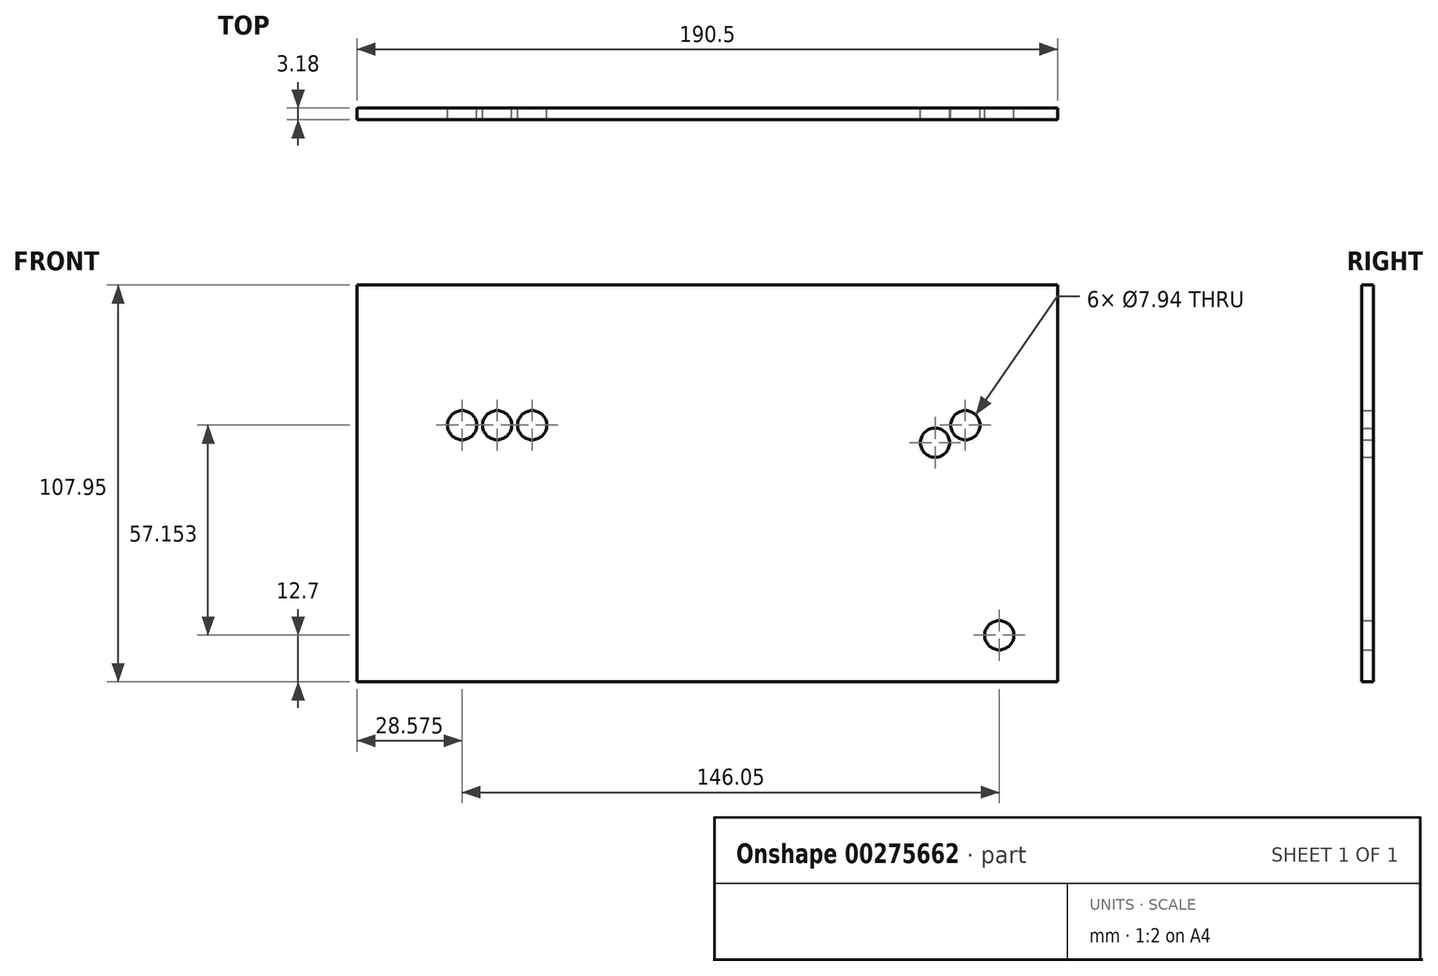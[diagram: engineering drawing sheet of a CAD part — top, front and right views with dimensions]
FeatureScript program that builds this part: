
annotation { "Feature Type Name" : "Feature", "Feature Type Description" : "" }
export const myFeature = defineFeature(function(context is Context, id is Id, definition is map)
    precondition{}
    {
        {
            var Q0;
            Q0=qCreatedBy(makeId("Front.planeOp"),FACE);
            var sketch = newSketch(context, id + "F0", { "sketchPlane" : qUnion([Q0])});
            skLineSegment(sketch, "E0.bottom", {"start": v(0, 0) * mm, "end": v(190.5, 0) * mm});
            skLineSegment(sketch, "E0.top", {"start": v(0, -107.95) * mm, "end": v(190.5, -107.95) * mm});
            skLineSegment(sketch, "E0.left", {"start": v(0, 0) * mm, "end": v(0, -107.95) * mm});
            skLineSegment(sketch, "E0.right", {"start": v(190.5, 0) * mm, "end": v(190.5, -107.95) * mm});
            skLineSegment(sketch, "E1", {"start": v(-10.1, -38.1) * mm, "end": v(60.63, -38.1) * mm, "construction": true});
            skLineSegment(sketch, "E2", {"start": v(38.1, -32.24) * mm, "end": v(38.1, -45.82) * mm, "construction": true});
            skCircle(sketch, "E3", {"center": v(38.1, -38.1) * mm, "radius": 3.97 * mm});
            skLineSegment(sketch, "E4", {"start": v(28.58, -32.24) * mm, "end": v(28.58, -45.82) * mm, "construction": true});
            skCircle(sketch, "E5", {"center": v(28.58, -38.1) * mm, "radius": 3.97 * mm});
            skLineSegment(sketch, "E6", {"start": v(47.63, -32.24) * mm, "end": v(47.63, -45.82) * mm, "construction": true});
            skCircle(sketch, "E7", {"center": v(47.63, -38.1) * mm, "radius": 3.97 * mm});
            skPoint(sketch, "E7.centerSnap0", {"position": v(47.63, -39.03) * mm});
            skLineSegment(sketch, "E8", {"start": v(157.16, -21.46) * mm, "end": v(157.16, -56.36) * mm, "construction": true});
            skLineSegment(sketch, "E9", {"start": v(140.45, -42.86) * mm, "end": v(174.03, -42.86) * mm, "construction": true});
            skCircle(sketch, "E10", {"center": v(157.16, -42.86) * mm, "radius": 3.97 * mm});
            skLineSegment(sketch, "E11", {"start": v(157.16, -42.86) * mm, "end": v(190.5, -23.6) * mm, "construction": true});
            skCircle(sketch, "E12", {"center": v(38.1, -38.1) * mm, "radius": 15.88 * mm, "construction": true});
            skCircle(sketch, "E13", {"center": v(38.1, -38.1) * mm, "radius": 19.05 * mm, "construction": true});
            skCircle(sketch, "E14", {"center": v(38.1, -38.1) * mm, "radius": 34.93 * mm, "construction": true});
            skCircle(sketch, "E15", {"center": v(38.1, -38.1) * mm, "radius": 38.1 * mm, "construction": true});
            skLineSegment(sketch, "E16", {"start": v(162.15, -32.45) * mm, "end": v(165.4, -38.1) * mm, "construction": true});
            skLineSegment(sketch, "E17", {"start": v(157.16, -42.86) * mm, "end": v(153.44, -36.42) * mm, "construction": true});
            skCircle(sketch, "E18", {"center": v(165.4, -38.1) * mm, "radius": 3.97 * mm});
            skLineSegment(sketch, "E19", {"start": v(174.62, -87.84) * mm, "end": v(174.62, -103.57) * mm, "construction": true});
            skLineSegment(sketch, "E20", {"start": v(164.27, -95.25) * mm, "end": v(183.18, -95.25) * mm, "construction": true});
            skCircle(sketch, "E21", {"center": v(174.62, -95.25) * mm, "radius": 3.97 * mm});
            skSolve(sketch);
        }
        {
            var Q0;
            Q0=makeQuery(id+"F0.imprint","IMPRINT",FACE,{"disambiguationData":[TD([[makeQuery(id+"F0.imprint","IMPRINT",EDGE,{"derivedFrom":sQuery(id+"F0.wireOp",EDGE,"E0.bottom")}),-1.0]])]});
            extrude(context, id + "F1", {"entities" : qUnion([Q0]), "depth" : 3.17 * mm});
        }
    });
